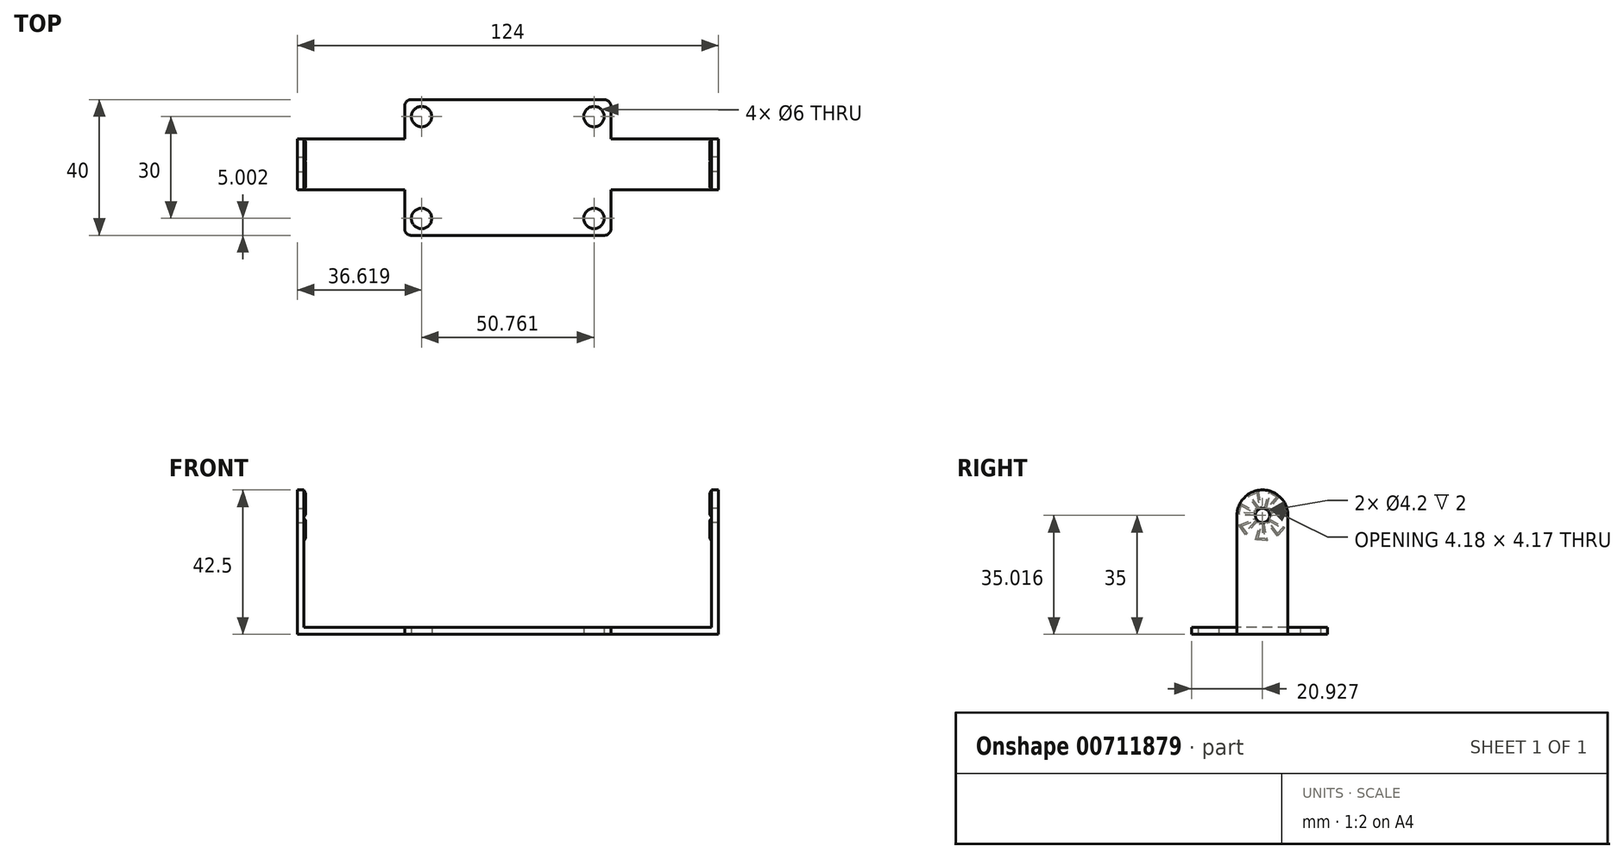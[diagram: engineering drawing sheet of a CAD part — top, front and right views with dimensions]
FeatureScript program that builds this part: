
annotation { "Feature Type Name" : "Feature", "Feature Type Description" : "" }
export const myFeature = defineFeature(function(context is Context, id is Id, definition is map)
    precondition{}
    {
        {
            var Q0;
            Q0=qCreatedBy(makeId("Top.planeOp"),FACE);
            var sketch = newSketch(context, id + "F0", { "sketchPlane" : qUnion([Q0])});
            skLineSegment(sketch, "E0.bottom", {"start": v(-28.38, 20.42) * mm, "end": v(0, 20.42) * mm});
            skLineSegment(sketch, "E0.top", {"start": v(-28.38, -19.58) * mm, "end": v(0, -19.58) * mm});
            skLineSegment(sketch, "E0.left", {"start": v(-30.38, 18.42) * mm, "end": v(-30.38, -17.58) * mm});
            skCircle(sketch, "E1", {"center": v(-25.38, 15.42) * mm, "radius": 3 * mm});
            skCircle(sketch, "E2", {"center": v(-25.38, -14.58) * mm, "radius": 3 * mm});
            skPoint(sketch, "E3.visualSharp", {"position": v(-30.38, 20.42) * mm});
            skArc(sketch, "E3.filletArc", {"start": v(-28.38, 20.42) * mm, "mid": v(-29.8, 19.84) * mm, "end": v(-30.38, 18.42) * mm});
            skPoint(sketch, "E4.visualSharp", {"position": v(30.62, 20.42) * mm});
            skPoint(sketch, "E5.visualSharp", {"position": v(-30.38, -19.58) * mm});
            skArc(sketch, "E5.filletArc", {"start": v(-30.38, -17.58) * mm, "mid": v(-29.8, -19) * mm, "end": v(-28.38, -19.58) * mm});
            skPoint(sketch, "E6.visualSharp", {"position": v(30.62, -19.58) * mm});
            skLineSegment(sketch, "E7", {"start": v(0, 20.42) * mm, "end": v(0, -19.58) * mm});
            skPoint(sketch, "E8.center.orphan", {"position": v(25.62, 15.42) * mm});
            skPoint(sketch, "E9.center.orphan", {"position": v(25.62, -14.58) * mm});
            skSolve(sketch);
        }
        {
            var Q0;
            Q0=qSketchRegion(id+"FlYgRnEniIu7ZzQ_0",true);
            var Q1;
            Q1=makeQuery(id+"F0.imprint","IMPRINT",FACE,{"disambiguationData":[TD([[makeQuery(id+"F0.imprint","IMPRINT",EDGE,{"derivedFrom":sQuery(id+"F0.wireOp",EDGE,"E0.bottom")}),-1.0]])]});
            extrude(context, id + "F1", {"entities" : qUnion([Q0, Q1]), "depth" : 2 * mm, "offsetDistance" : 25.4 * mm});
        }
        {
            var Q0;
            Q0=makeQuery(id+"F1.opExtrude","CAP_FACE",FACE,{"disambiguationData":[OSD([sQuery(id+"F0.wireOp",EDGE,"E0.bottom"),sQuery(id+"F0.wireOp",EDGE,"E0.top"),sQuery(id+"F0.wireOp",EDGE,"E0.left"),sQuery(id+"F0.wireOp",EDGE,"E0.right"),sQuery(id+"F0.wireOp",EDGE,"E1"),sQuery(id+"F0.wireOp",EDGE,"E2"),sQuery(id+"F0.wireOp",EDGE,"E8"),sQuery(id+"F0.wireOp",EDGE,"E9"),sQuery(id+"F0.wireOp",EDGE,"E3.filletArc"),sQuery(id+"F0.wireOp",EDGE,"E4.filletArc"),sQuery(id+"F0.wireOp",EDGE,"E5.filletArc"),sQuery(id+"F0.wireOp",EDGE,"E6.filletArc")])],"isStart":false});
            var sketch = newSketch(context, id + "F2", { "sketchPlane" : qUnion([Q0])});
            skPoint(sketch, "E10.middle", {"position": v(0, 0) * mm});
            skPoint(sketch, "E10.right.start.orphan", {"position": v(15, 9) * mm});
            skPoint(sketch, "E10.top.end.orphan", {"position": v(15, -9) * mm});
            skPoint(sketch, "E10.left.end.orphan", {"position": v(-15, -9) * mm});
            skPoint(sketch, "E10.left.start.orphan", {"position": v(-15, 9) * mm});
            skSolve(sketch);
        }
        {
            var Q0;
            Q0=makeQuery(id+"F2.imprint","IMPRINT",FACE,{"disambiguationData":[TD([[makeQuery(id+"F2.imprint","IMPRINT",EDGE,{"derivedFrom":makeQuery(id+"F1.opExtrude","CAP_EDGE",EDGE,{"disambiguationData":[OSD([sQuery(id+"F0.wireOp",EDGE,"E0.bottom")])],"isStart":false})}),-1.0]])]});
            var sketch = newSketch(context, id + "F3", { "sketchPlane" : qUnion([Q0])});
            skLineSegment(sketch, "E11", {"start": v(0, -35.95) * mm, "end": v(0, 40.93) * mm});
            skLineSegment(sketch, "E12", {"start": v(69.88, 0) * mm, "end": v(-86.86, 0) * mm});
            skLineSegment(sketch, "E13", {"start": v(0, 8.85) * mm, "end": v(-60, 8.85) * mm});
            skLineSegment(sketch, "E14", {"start": v(-60, 8.85) * mm, "end": v(-60, -6.15) * mm});
            skLineSegment(sketch, "E15", {"start": v(-60, -6.15) * mm, "end": v(0, -6.15) * mm});
            skSolve(sketch);
        }
        {
            var Q0;
            {var subQ0=sQuery(id+"F3.wireOp",EDGE,"E14");var subQ1=sQuery(id+"F3.wireOp",EDGE,"E12");var subQ2=makeQuery(id+"F3.imprint","INTERSECT",VERTEX,{"derivedFrom":[subQ1,subQ0]});Q0=makeQuery(id+"F3.imprint","IMPRINT",FACE,{"disambiguationData":[TD([[makeQuery(id+"F3.imprint","IMPRINT",EDGE,{"disambiguationData":[TD([[subQ2,1.0]])],"derivedFrom":subQ1}),-1.0]])]});}
            var Q1;
            {var subQ0=sQuery(id+"F3.wireOp",EDGE,"E14");var subQ1=sQuery(id+"F3.wireOp",EDGE,"E12");var subQ2=makeQuery(id+"F3.imprint","INTERSECT",VERTEX,{"derivedFrom":[subQ1,subQ0]});Q1=makeQuery(id+"F3.imprint","IMPRINT",FACE,{"disambiguationData":[TD([[makeQuery(id+"F3.imprint","IMPRINT",EDGE,{"disambiguationData":[TD([[subQ2,1.0]])],"derivedFrom":subQ1}),1.0]])]});}
            extrude(context, id + "F4", {"entities" : qUnion([Q0, Q1]), "operationType" : NewBodyOperationType.ADD, "oppositeDirection" : true, "depth" : 2 * mm, "offsetDistance" : 25 * mm});
        }
        {
            var Q0;
            Q0=makeQuery(id+"F4.opExtrude","SWEPT_FACE",FACE,{"disambiguationData":[OSD([sQuery(id+"F3.wireOp",EDGE,"E14")])]});
            var sketch = newSketch(context, id + "F5", { "sketchPlane" : qUnion([Q0])});
            skCircle(sketch, "E16", {"center": v(-1.35, 35) * mm, "radius": 7.5 * mm});
            skLineSegment(sketch, "E17", {"start": v(6.15, 2) * mm, "end": v(6.15, 35) * mm});
            skLineSegment(sketch, "E18.MirrorCS", {"start": v(-8.85, 2) * mm, "end": v(-8.85, 35) * mm});
            skCircle(sketch, "E19", {"center": v(-1.35, 35) * mm, "radius": 2.1 * mm});
            skCircle(sketch, "E20.cCircle", {"center": v(-1.35, 35) * mm, "radius": 7.5 * mm, "construction": true});
            skPoint(sketch, "E21.start.orphan", {"position": v(-1.35, 0) * mm});
            skLineSegment(sketch, "E22.0", {"start": v(5.56, 32.09) * mm, "end": v(3.61, 29.38) * mm});
            skLineSegment(sketch, "E22.1", {"start": v(3.61, 29.38) * mm, "end": v(0.68, 27.78) * mm});
            skLineSegment(sketch, "E22.2", {"start": v(0.68, 27.78) * mm, "end": v(-2.65, 27.61) * mm});
            skLineSegment(sketch, "E22.3", {"start": v(-2.65, 27.61) * mm, "end": v(-5.73, 28.91) * mm});
            skLineSegment(sketch, "E22.4", {"start": v(-5.73, 28.91) * mm, "end": v(-7.93, 31.41) * mm});
            skLineSegment(sketch, "E22.5", {"start": v(-7.93, 31.41) * mm, "end": v(-8.84, 34.63) * mm});
            skLineSegment(sketch, "E22.6", {"start": v(-8.84, 34.63) * mm, "end": v(-8.26, 37.91) * mm});
            skLineSegment(sketch, "E22.7", {"start": v(-8.26, 37.91) * mm, "end": v(-6.3, 40.62) * mm});
            skLineSegment(sketch, "E22.8", {"start": v(-6.3, 40.62) * mm, "end": v(-3.38, 42.22) * mm});
            skLineSegment(sketch, "E22.9", {"start": v(-3.38, 42.22) * mm, "end": v(-0.04, 42.39) * mm});
            skLineSegment(sketch, "E22.10", {"start": v(-0.04, 42.39) * mm, "end": v(3.03, 41.09) * mm});
            skLineSegment(sketch, "E22.11", {"start": v(3.03, 41.09) * mm, "end": v(5.24, 38.59) * mm});
            skLineSegment(sketch, "E22.12", {"start": v(5.24, 38.59) * mm, "end": v(6.14, 35.37) * mm});
            skLineSegment(sketch, "E22.13", {"start": v(6.14, 35.37) * mm, "end": v(5.56, 32.09) * mm});
            skLineSegment(sketch, "E23", {"start": v(-1.35, 35) * mm, "end": v(5.56, 32.09) * mm});
            skLineSegment(sketch, "E24", {"start": v(-1.35, 35) * mm, "end": v(-8.26, 37.91) * mm});
            skLineSegment(sketch, "E25", {"start": v(3.61, 29.38) * mm, "end": v(-6.3, 40.62) * mm});
            skLineSegment(sketch, "E26", {"start": v(-3.38, 42.22) * mm, "end": v(0.68, 27.78) * mm});
            skLineSegment(sketch, "E27", {"start": v(-0.04, 42.39) * mm, "end": v(-2.65, 27.61) * mm});
            skLineSegment(sketch, "E28", {"start": v(3.03, 41.09) * mm, "end": v(-5.73, 28.91) * mm});
            skLineSegment(sketch, "E29", {"start": v(5.24, 38.59) * mm, "end": v(-7.93, 31.41) * mm});
            skLineSegment(sketch, "E30", {"start": v(6.14, 35.37) * mm, "end": v(-8.84, 34.63) * mm});
            skSolve(sketch);
        }
        {
            var Q0;
            {var subQ1=sQuery(id+"F5.wireOp",EDGE,"E17");Q0=makeQuery(id+"F5.imprint","IMPRINT",FACE,{"disambiguationData":[TD([[makeQuery(id+"F5.imprint","IMPRINT",EDGE,{"derivedFrom":subQ1}),1.0]])]});}
            var Q1;
            {var subQ10=sQuery(id+"F5.wireOp",EDGE,"E20.0");Q1=makeQuery(id+"F5.imprint","IMPRINT",FACE,{"disambiguationData":[TD([[makeQuery(id+"F5.imprint","IMPRINT",EDGE,{"derivedFrom":subQ10}),-1.0]])]});}
            var Q2;
            {var subQ5=sQuery(id+"F5.wireOp",EDGE,"E20.14");Q2=makeQuery(id+"F5.imprint","IMPRINT",FACE,{"disambiguationData":[TD([[makeQuery(id+"F5.imprint","IMPRINT",EDGE,{"derivedFrom":subQ5}),-1.0]])]});}
            var Q3;
            {var subQ0=sQuery(id+"F5.wireOp",EDGE,"E20.0");Q3=makeQuery(id+"F5.imprint","IMPRINT",FACE,{"disambiguationData":[TD([[makeQuery(id+"F5.imprint","IMPRINT",EDGE,{"derivedFrom":subQ0}),1.0]])]});}
            var Q4;
            {var subQ0=sQuery(id+"F5.wireOp",EDGE,"E20.1");Q4=makeQuery(id+"F5.imprint","IMPRINT",FACE,{"disambiguationData":[TD([[makeQuery(id+"F5.imprint","IMPRINT",EDGE,{"derivedFrom":subQ0}),1.0]])]});}
            var Q5;
            {var subQ0=sQuery(id+"F5.wireOp",EDGE,"E20.2");Q5=makeQuery(id+"F5.imprint","IMPRINT",FACE,{"disambiguationData":[TD([[makeQuery(id+"F5.imprint","IMPRINT",EDGE,{"derivedFrom":subQ0}),1.0]])]});}
            var Q6;
            {var subQ0=sQuery(id+"F5.wireOp",EDGE,"E20.14");Q6=makeQuery(id+"F5.imprint","IMPRINT",FACE,{"disambiguationData":[TD([[makeQuery(id+"F5.imprint","IMPRINT",EDGE,{"derivedFrom":subQ0}),1.0]])]});}
            var Q7;
            {var subQ0=sQuery(id+"F5.wireOp",EDGE,"E20.13");Q7=makeQuery(id+"F5.imprint","IMPRINT",FACE,{"disambiguationData":[TD([[makeQuery(id+"F5.imprint","IMPRINT",EDGE,{"derivedFrom":subQ0}),1.0]])]});}
            var Q8;
            {var subQ0=sQuery(id+"F5.wireOp",EDGE,"E20.5");Q8=makeQuery(id+"F5.imprint","IMPRINT",FACE,{"disambiguationData":[TD([[makeQuery(id+"F5.imprint","IMPRINT",EDGE,{"derivedFrom":subQ0}),1.0]])]});}
            var Q9;
            {var subQ0=sQuery(id+"F5.wireOp",EDGE,"rMBlOFN2-h6bl-RFFZ-SnFr-eubzp8ZbVUaf");var subQ3=sQuery(id+"F5.wireOp",EDGE,"E20.4");var subQ5=makeQuery(id+"F5.imprint","INTERSECT",VERTEX,{"derivedFrom":[subQ0,subQ3]});Q9=makeQuery(id+"F5.imprint","IMPRINT",FACE,{"disambiguationData":[TD([[makeQuery(id+"F5.imprint","IMPRINT",EDGE,{"disambiguationData":[TD([[subQ5,-1.0]])],"derivedFrom":subQ0}),-1.0]])]});}
            var Q10;
            {var subQ0=sQuery(id+"F5.wireOp",EDGE,"rMBlOFN2-h6bl-RFFZ-SnFr-eubzp8ZbVUaf");var subQ3=sQuery(id+"F5.wireOp",EDGE,"E20.4");var subQ5=makeQuery(id+"F5.imprint","INTERSECT",VERTEX,{"derivedFrom":[subQ0,subQ3]});Q10=makeQuery(id+"F5.imprint","IMPRINT",FACE,{"disambiguationData":[TD([[makeQuery(id+"F5.imprint","IMPRINT",EDGE,{"disambiguationData":[TD([[subQ5,-1.0]])],"derivedFrom":subQ0}),1.0]])]});}
            var Q11;
            {var subQ0=sQuery(id+"F5.wireOp",EDGE,"E20.6");Q11=makeQuery(id+"F5.imprint","IMPRINT",FACE,{"disambiguationData":[TD([[makeQuery(id+"F5.imprint","IMPRINT",EDGE,{"derivedFrom":subQ0}),1.0]])]});}
            var Q12;
            {var subQ0=sQuery(id+"F5.wireOp",EDGE,"E20.7");Q12=makeQuery(id+"F5.imprint","IMPRINT",FACE,{"disambiguationData":[TD([[makeQuery(id+"F5.imprint","IMPRINT",EDGE,{"derivedFrom":subQ0}),1.0]])]});}
            var Q13;
            {var subQ0=sQuery(id+"F5.wireOp",EDGE,"E20.12");Q13=makeQuery(id+"F5.imprint","IMPRINT",FACE,{"disambiguationData":[TD([[makeQuery(id+"F5.imprint","IMPRINT",EDGE,{"derivedFrom":subQ0}),1.0]])]});}
            var Q14;
            {var subQ2=sQuery(id+"F5.wireOp",EDGE,"E20.11");Q14=makeQuery(id+"F5.imprint","IMPRINT",FACE,{"disambiguationData":[TD([[makeQuery(id+"F5.imprint","IMPRINT",EDGE,{"derivedFrom":subQ2}),1.0]])]});}
            var Q15;
            {var subQ0=sQuery(id+"F5.wireOp",EDGE,"E20.10");Q15=makeQuery(id+"F5.imprint","IMPRINT",FACE,{"disambiguationData":[TD([[makeQuery(id+"F5.imprint","IMPRINT",EDGE,{"derivedFrom":subQ0}),1.0]])]});}
            var Q16;
            {var subQ0=sQuery(id+"F5.wireOp",EDGE,"E20.9");Q16=makeQuery(id+"F5.imprint","IMPRINT",FACE,{"disambiguationData":[TD([[makeQuery(id+"F5.imprint","IMPRINT",EDGE,{"derivedFrom":subQ0}),1.0]])]});}
            var Q17;
            {var subQ0=sQuery(id+"F5.wireOp",EDGE,"E20.8");Q17=makeQuery(id+"F5.imprint","IMPRINT",FACE,{"disambiguationData":[TD([[makeQuery(id+"F5.imprint","IMPRINT",EDGE,{"derivedFrom":subQ0}),1.0]])]});}
            var Q18;
            {var subQ5=sQuery(id+"F5.wireOp",EDGE,"E20.1");Q18=makeQuery(id+"F5.imprint","IMPRINT",FACE,{"disambiguationData":[TD([[makeQuery(id+"F5.imprint","IMPRINT",EDGE,{"derivedFrom":subQ5}),-1.0]])]});}
            var Q19;
            {var subQ5=sQuery(id+"F5.wireOp",EDGE,"E20.2");Q19=makeQuery(id+"F5.imprint","IMPRINT",FACE,{"disambiguationData":[TD([[makeQuery(id+"F5.imprint","IMPRINT",EDGE,{"derivedFrom":subQ5}),-1.0]])]});}
            var Q20;
            {var subQ5=sQuery(id+"F5.wireOp",EDGE,"E20.3");Q20=makeQuery(id+"F5.imprint","IMPRINT",FACE,{"disambiguationData":[TD([[makeQuery(id+"F5.imprint","IMPRINT",EDGE,{"derivedFrom":subQ5}),-1.0]])]});}
            var Q21;
            {var subQ0=sQuery(id+"F5.wireOp",EDGE,"hJvx8XM6-hgbs-Rpk0-bUnE-3N1nT94Q1vuU");var subQ4=sQuery(id+"F5.wireOp",EDGE,"E19");var subQ5=makeQuery(id+"F5.imprint","INTERSECT",VERTEX,{"derivedFrom":[subQ4,subQ0]});Q21=makeQuery(id+"F5.imprint","IMPRINT",FACE,{"disambiguationData":[TD([[makeQuery(id+"F5.imprint","IMPRINT",EDGE,{"disambiguationData":[TD([[subQ5,1.0]])],"derivedFrom":subQ4}),-1.0]])]});}
            var Q22;
            {var subQ5=sQuery(id+"F5.wireOp",EDGE,"E20.5");Q22=makeQuery(id+"F5.imprint","IMPRINT",FACE,{"disambiguationData":[TD([[makeQuery(id+"F5.imprint","IMPRINT",EDGE,{"derivedFrom":subQ5}),-1.0]])]});}
            var Q23;
            {var subQ5=sQuery(id+"F5.wireOp",EDGE,"E20.6");Q23=makeQuery(id+"F5.imprint","IMPRINT",FACE,{"disambiguationData":[TD([[makeQuery(id+"F5.imprint","IMPRINT",EDGE,{"derivedFrom":subQ5}),-1.0]])]});}
            var Q24;
            {var subQ5=sQuery(id+"F5.wireOp",EDGE,"E20.7");Q24=makeQuery(id+"F5.imprint","IMPRINT",FACE,{"disambiguationData":[TD([[makeQuery(id+"F5.imprint","IMPRINT",EDGE,{"derivedFrom":subQ5}),-1.0]])]});}
            var Q25;
            {var subQ5=sQuery(id+"F5.wireOp",EDGE,"E20.8");Q25=makeQuery(id+"F5.imprint","IMPRINT",FACE,{"disambiguationData":[TD([[makeQuery(id+"F5.imprint","IMPRINT",EDGE,{"derivedFrom":subQ5}),-1.0]])]});}
            var Q26;
            {var subQ5=sQuery(id+"F5.wireOp",EDGE,"E20.9");Q26=makeQuery(id+"F5.imprint","IMPRINT",FACE,{"disambiguationData":[TD([[makeQuery(id+"F5.imprint","IMPRINT",EDGE,{"derivedFrom":subQ5}),-1.0]])]});}
            var Q27;
            {var subQ5=sQuery(id+"F5.wireOp",EDGE,"E20.10");Q27=makeQuery(id+"F5.imprint","IMPRINT",FACE,{"disambiguationData":[TD([[makeQuery(id+"F5.imprint","IMPRINT",EDGE,{"derivedFrom":subQ5}),-1.0]])]});}
            var Q28;
            {var subQ5=sQuery(id+"F5.wireOp",EDGE,"E20.11");Q28=makeQuery(id+"F5.imprint","IMPRINT",FACE,{"disambiguationData":[TD([[makeQuery(id+"F5.imprint","IMPRINT",EDGE,{"derivedFrom":subQ5}),-1.0]])]});}
            var Q29;
            {var subQ5=sQuery(id+"F5.wireOp",EDGE,"E20.12");Q29=makeQuery(id+"F5.imprint","IMPRINT",FACE,{"disambiguationData":[TD([[makeQuery(id+"F5.imprint","IMPRINT",EDGE,{"derivedFrom":subQ5}),-1.0]])]});}
            var Q30;
            {var subQ5=sQuery(id+"F5.wireOp",EDGE,"E20.13");Q30=makeQuery(id+"F5.imprint","IMPRINT",FACE,{"disambiguationData":[TD([[makeQuery(id+"F5.imprint","IMPRINT",EDGE,{"derivedFrom":subQ5}),-1.0]])]});}
            var Q31;
            {var subQ0=sQuery(id+"F5.wireOp",EDGE,"E20.3");Q31=makeQuery(id+"F5.imprint","IMPRINT",FACE,{"disambiguationData":[TD([[makeQuery(id+"F5.imprint","IMPRINT",EDGE,{"derivedFrom":subQ0}),1.0]])]});}
            var Q32;
            {var subQ2=sQuery(id+"F5.wireOp",EDGE,"E20.4");Q32=makeQuery(id+"F5.imprint","IMPRINT",FACE,{"disambiguationData":[TD([[makeQuery(id+"F5.imprint","IMPRINT",EDGE,{"derivedFrom":subQ2}),1.0]])]});}
            var Q33;
            {var subQ0=sQuery(id+"F5.wireOp",EDGE,"E22.5");Q33=makeQuery(id+"F5.imprint","IMPRINT",FACE,{"disambiguationData":[TD([[makeQuery(id+"F5.imprint","IMPRINT",EDGE,{"derivedFrom":subQ0}),1.0]])]});}
            var Q34;
            {var subQ0=sQuery(id+"F5.wireOp",EDGE,"E22.4");Q34=makeQuery(id+"F5.imprint","IMPRINT",FACE,{"disambiguationData":[TD([[makeQuery(id+"F5.imprint","IMPRINT",EDGE,{"derivedFrom":subQ0}),1.0]])]});}
            var Q35;
            {var subQ2=sQuery(id+"F5.wireOp",EDGE,"E22.13");Q35=makeQuery(id+"F5.imprint","IMPRINT",FACE,{"disambiguationData":[TD([[makeQuery(id+"F5.imprint","IMPRINT",EDGE,{"derivedFrom":subQ2}),1.0]])]});}
            var Q36;
            {var subQ0=sQuery(id+"F5.wireOp",EDGE,"E22.0");Q36=makeQuery(id+"F5.imprint","IMPRINT",FACE,{"disambiguationData":[TD([[makeQuery(id+"F5.imprint","IMPRINT",EDGE,{"derivedFrom":subQ0}),1.0]])]});}
            var Q37;
            {var subQ0=sQuery(id+"F5.wireOp",EDGE,"E22.3");Q37=makeQuery(id+"F5.imprint","IMPRINT",FACE,{"disambiguationData":[TD([[makeQuery(id+"F5.imprint","IMPRINT",EDGE,{"derivedFrom":subQ0}),1.0]])]});}
            var Q38;
            {var subQ0=sQuery(id+"F5.wireOp",EDGE,"E22.2");Q38=makeQuery(id+"F5.imprint","IMPRINT",FACE,{"disambiguationData":[TD([[makeQuery(id+"F5.imprint","IMPRINT",EDGE,{"derivedFrom":subQ0}),1.0]])]});}
            var Q39;
            {var subQ0=sQuery(id+"F5.wireOp",EDGE,"E22.1");Q39=makeQuery(id+"F5.imprint","IMPRINT",FACE,{"disambiguationData":[TD([[makeQuery(id+"F5.imprint","IMPRINT",EDGE,{"derivedFrom":subQ0}),1.0]])]});}
            var Q40;
            {var subQ0=sQuery(id+"F5.wireOp",EDGE,"E22.12");Q40=makeQuery(id+"F5.imprint","IMPRINT",FACE,{"disambiguationData":[TD([[makeQuery(id+"F5.imprint","IMPRINT",EDGE,{"derivedFrom":subQ0}),1.0]])]});}
            var Q41;
            {var subQ2=sQuery(id+"F5.wireOp",EDGE,"E22.6");Q41=makeQuery(id+"F5.imprint","IMPRINT",FACE,{"disambiguationData":[TD([[makeQuery(id+"F5.imprint","IMPRINT",EDGE,{"derivedFrom":subQ2}),1.0]])]});}
            var Q42;
            {var subQ0=sQuery(id+"F5.wireOp",EDGE,"E22.7");Q42=makeQuery(id+"F5.imprint","IMPRINT",FACE,{"disambiguationData":[TD([[makeQuery(id+"F5.imprint","IMPRINT",EDGE,{"derivedFrom":subQ0}),1.0]])]});}
            var Q43;
            {var subQ0=sQuery(id+"F5.wireOp",EDGE,"E22.8");Q43=makeQuery(id+"F5.imprint","IMPRINT",FACE,{"disambiguationData":[TD([[makeQuery(id+"F5.imprint","IMPRINT",EDGE,{"derivedFrom":subQ0}),1.0]])]});}
            var Q44;
            {var subQ0=sQuery(id+"F5.wireOp",EDGE,"E22.9");Q44=makeQuery(id+"F5.imprint","IMPRINT",FACE,{"disambiguationData":[TD([[makeQuery(id+"F5.imprint","IMPRINT",EDGE,{"derivedFrom":subQ0}),1.0]])]});}
            var Q45;
            {var subQ0=sQuery(id+"F5.wireOp",EDGE,"E22.10");Q45=makeQuery(id+"F5.imprint","IMPRINT",FACE,{"disambiguationData":[TD([[makeQuery(id+"F5.imprint","IMPRINT",EDGE,{"derivedFrom":subQ0}),1.0]])]});}
            var Q46;
            {var subQ0=sQuery(id+"F5.wireOp",EDGE,"E22.11");Q46=makeQuery(id+"F5.imprint","IMPRINT",FACE,{"disambiguationData":[TD([[makeQuery(id+"F5.imprint","IMPRINT",EDGE,{"derivedFrom":subQ0}),1.0]])]});}
            extrude(context, id + "F6", {"entities" : qUnion([Q0, Q1, Q2, Q3, Q4, Q5, Q6, Q7, Q8, Q9, Q10, Q11, Q12, Q13, Q14, Q15, Q16, Q17, Q18, Q19, Q20, Q21, Q22, Q23, Q24, Q25, Q26, Q27, Q28, Q29, Q30, Q31, Q32, Q33, Q34, Q35, Q36, Q37, Q38, Q39, Q40, Q41, Q42, Q43, Q44, Q45, Q46]), "depth" : 2 * mm, "offsetDistance" : 25 * mm});
        }
        {
            var Q0;
            Q0=makeQuery(id+"F4.opExtrude","SWEPT_FACE",FACE,{"disambiguationData":[OSD([sQuery(id+"F3.wireOp",EDGE,"E14")])]});
            extrude(context, id + "F7", {"entities" : qUnion([Q0]), "operationType" : NewBodyOperationType.ADD, "depth" : 2 * mm, "offsetDistance" : 25 * mm});
        }
        {
            var Q0;
            {var subQ5=sQuery(id+"F5.wireOp",EDGE,"E22.0");Q0=makeQuery(id+"F5.imprint","IMPRINT",FACE,{"disambiguationData":[TD([[makeQuery(id+"F5.imprint","IMPRINT",EDGE,{"derivedFrom":subQ5}),-1.0]])]});}
            var Q1;
            {var subQ5=sQuery(id+"F5.wireOp",EDGE,"E22.12");Q1=makeQuery(id+"F5.imprint","IMPRINT",FACE,{"disambiguationData":[TD([[makeQuery(id+"F5.imprint","IMPRINT",EDGE,{"derivedFrom":subQ5}),-1.0]])]});}
            var Q2;
            {var subQ5=sQuery(id+"F5.wireOp",EDGE,"E22.10");Q2=makeQuery(id+"F5.imprint","IMPRINT",FACE,{"disambiguationData":[TD([[makeQuery(id+"F5.imprint","IMPRINT",EDGE,{"derivedFrom":subQ5}),-1.0]])]});}
            var Q3;
            {var subQ5=sQuery(id+"F5.wireOp",EDGE,"E22.8");Q3=makeQuery(id+"F5.imprint","IMPRINT",FACE,{"disambiguationData":[TD([[makeQuery(id+"F5.imprint","IMPRINT",EDGE,{"derivedFrom":subQ5}),-1.0]])]});}
            var Q4;
            {var subQ5=sQuery(id+"F5.wireOp",EDGE,"E22.6");Q4=makeQuery(id+"F5.imprint","IMPRINT",FACE,{"disambiguationData":[TD([[makeQuery(id+"F5.imprint","IMPRINT",EDGE,{"derivedFrom":subQ5}),-1.0]])]});}
            var Q5;
            {var subQ5=sQuery(id+"F5.wireOp",EDGE,"E22.4");Q5=makeQuery(id+"F5.imprint","IMPRINT",FACE,{"disambiguationData":[TD([[makeQuery(id+"F5.imprint","IMPRINT",EDGE,{"derivedFrom":subQ5}),-1.0]])]});}
            var Q6;
            {var subQ5=sQuery(id+"F5.wireOp",EDGE,"E22.2");Q6=makeQuery(id+"F5.imprint","IMPRINT",FACE,{"disambiguationData":[TD([[makeQuery(id+"F5.imprint","IMPRINT",EDGE,{"derivedFrom":subQ5}),-1.0]])]});}
            extrude(context, id + "F8", {"entities" : qUnion([Q0, Q1, Q2, Q3, Q4, Q5, Q6]), "operationType" : NewBodyOperationType.ADD, "oppositeDirection" : true, "depth" : 0.5 * mm, "offsetDistance" : 25 * mm, "hasDraft" : true, "draftAngle" : 45 * degree, "draftPullDirection" : true});
        }
        {
            var Q0;
            Q0=makeQuery(id+"F7.opExtrude","SWEPT_BODY",BODY,{"disambiguationData":[OSD([sQuery(id+"F3.wireOp",EDGE,"E14")])]});
            var Q1;
            Q1=makeQuery(id+"F6.opExtrude","SWEPT_BODY",BODY,{"disambiguationData":[OSD([sQuery(id+"F3.wireOp",EDGE,"E14"),sQuery(id+"F5.wireOp",EDGE,"E16"),sQuery(id+"F5.wireOp",EDGE,"E17"),sQuery(id+"F5.wireOp",EDGE,"E18.MirrorCS"),sQuery(id+"F5.wireOp",EDGE,"E19")])]});
            var Q2;
            Q2=makeQuery(id+"F1.opExtrude","SWEPT_BODY",BODY,{"disambiguationData":[OSD([sQuery(id+"F0.wireOp",EDGE,"E0.bottom"),sQuery(id+"F0.wireOp",EDGE,"E0.top"),sQuery(id+"F0.wireOp",EDGE,"E0.left"),sQuery(id+"F0.wireOp",EDGE,"E1"),sQuery(id+"F0.wireOp",EDGE,"E2"),sQuery(id+"F0.wireOp",EDGE,"E3.filletArc"),sQuery(id+"F0.wireOp",EDGE,"E5.filletArc"),sQuery(id+"F0.wireOp",EDGE,"E7")])]});
            var Q3;
            Q3=qCreatedBy(makeId("Right.planeOp"),FACE);
            mirror(context, id + "F9", {"operationType" : NewBodyOperationType.ADD, "entities" : qUnion([Q0, Q1, Q2]), "mirrorPlane" : qUnion([Q3])});
        }
    });
